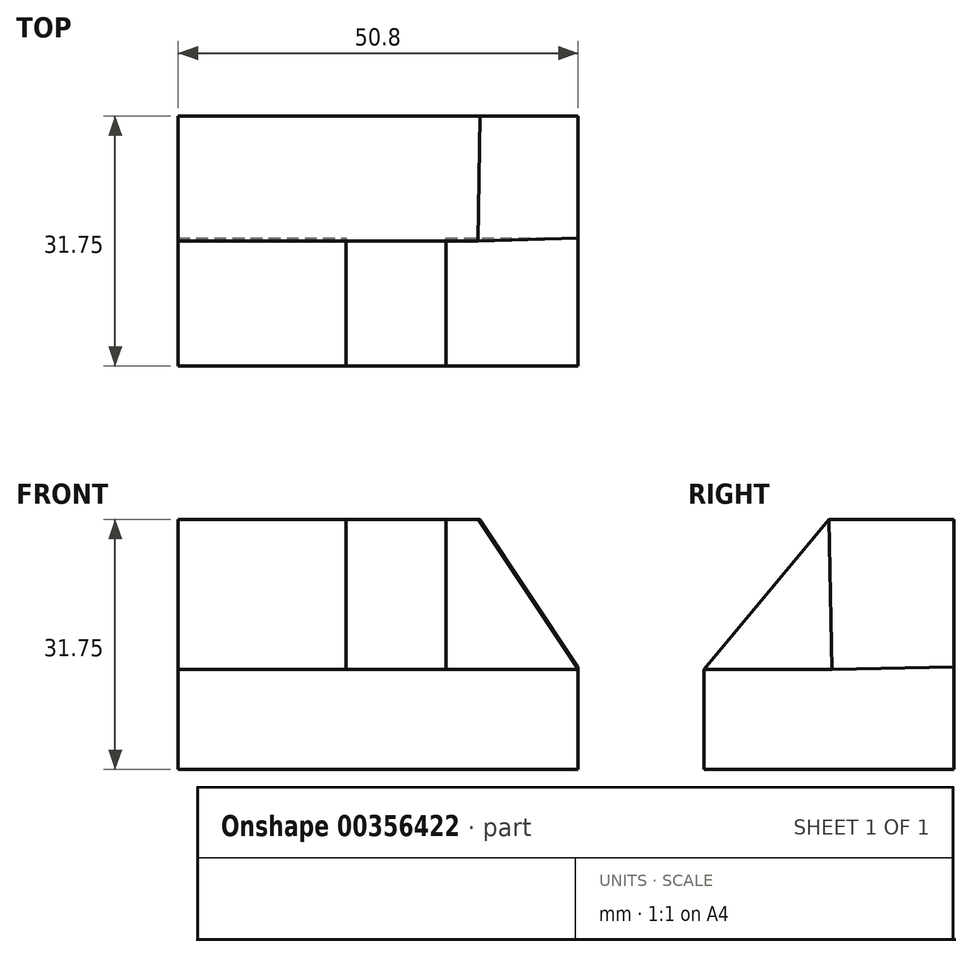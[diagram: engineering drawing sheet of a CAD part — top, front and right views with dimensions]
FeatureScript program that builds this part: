
annotation { "Feature Type Name" : "Feature", "Feature Type Description" : "" }
export const myFeature = defineFeature(function(context is Context, id is Id, definition is map)
    precondition{}
    {
        {
            var Q0;
            Q0=qCreatedBy(makeId("Front.planeOp"),FACE);
            var sketch = newSketch(context, id + "F0", { "sketchPlane" : qUnion([Q0])});
            skLineSegment(sketch, "E0", {"start": v(0, 31.75) * mm, "end": v(0, 0) * mm});
            skLineSegment(sketch, "E1", {"start": v(0, 0) * mm, "end": v(50.8, 0) * mm});
            skLineSegment(sketch, "E2", {"start": v(50.8, 0) * mm, "end": v(50.8, 31.75) * mm});
            skLineSegment(sketch, "E3", {"start": v(50.8, 31.75) * mm, "end": v(0, 31.75) * mm});
            skSolve(sketch);
        }
        {
            var Q0;
            Q0 = qSketchRegion(id + "F0", true);
            extrude(context, id + "F1", {"entities" : qUnion([Q0]), "depth" : 31.75 * mm});
        }
        {
            var Q0;
            Q0=makeQuery(id+"F1.opExtrude","SWEPT_FACE",FACE,{"disambiguationData":[OSD([sQuery(id+"F0.wireOp",EDGE,"E2")])]});
            var sketch = newSketch(context, id + "F2", { "sketchPlane" : qUnion([Q0])});
            skLineSegment(sketch, "E4", {"start": v(-31.75, 12.7) * mm, "end": v(-15.87, 31.75) * mm});
            skSolve(sketch);
        }
        {
            var Q0;
            Q0 = qSketchRegion(id + "F2", true);
            var Q1;
            {var subQ0=sQuery(id+"F2.wireOp",EDGE,"E4");Q1=makeQuery(id+"F2.imprint","IMPRINT",FACE,{"disambiguationData":[TD([[makeQuery(id+"F2.imprint","IMPRINT",EDGE,{"derivedFrom":subQ0}),1.0]])]});}
            extrude(context, id + "F3", {"entities" : qUnion([Q0, Q1]), "operationType" : NewBodyOperationType.REMOVE, "oppositeDirection" : true, "depth" : 50.8 * mm});
        }
        {
            var Q0;
            Q0=makeQuery(id+"F1.opExtrude","SWEPT_FACE",FACE,{"disambiguationData":[OSD([sQuery(id+"F0.wireOp",EDGE,"E2")])]});
            var sketch = newSketch(context, id + "F4", { "sketchPlane" : qUnion([Q0])});
            skLineSegment(sketch, "E5", {"start": v(-31.75, 12.7) * mm, "end": v(-15.48, 12.7) * mm});
            skLineSegment(sketch, "E6", {"start": v(-15.48, 12.7) * mm, "end": v(-15.88, 31.75) * mm});
            skSolve(sketch);
        }
        {
            var Q0;
            Q0=makeQuery(id+"F4.imprint","IMPRINT",FACE,{"disambiguationData":[TD([[makeQuery(id+"F4.imprint","IMPRINT",EDGE,{"derivedFrom":sQuery(id+"F4.wireOp",EDGE,"E5")}),1.0]])]});
            extrude(context, id + "F5", {"entities" : qUnion([Q0]), "operationType" : NewBodyOperationType.REMOVE, "oppositeDirection" : true, "depth" : 50.8 * mm});
        }
        {
            var Q0;
            Q0=makeQuery(id+"F5.boolean.opBoolean","COPY",FACE,{"derivedFrom":makeQuery(id+"F5.opExtrude","SWEPT_FACE",FACE,{"disambiguationData":[OSD([sQuery(id+"F4.wireOp",EDGE,"E6")])]})});
            var sketch = newSketch(context, id + "F6", { "sketchPlane" : qUnion([Q0])});
            skLineSegment(sketch, "E7", {"start": v(50.8, 13.02) * mm, "end": v(38.1, 32.08) * mm});
            skSolve(sketch);
        }
        {
            var Q0;
            Q0 = qSketchRegion(id + "F6", true);
            var Q1;
            {var subQ0=sQuery(id+"F6.wireOp",EDGE,"E7");Q1=makeQuery(id+"F6.imprint","IMPRINT",FACE,{"disambiguationData":[TD([[makeQuery(id+"F6.imprint","IMPRINT",EDGE,{"derivedFrom":subQ0}),-1.0]])]});}
            extrude(context, id + "F7", {"entities" : qUnion([Q0, Q1]), "operationType" : NewBodyOperationType.REMOVE, "oppositeDirection" : true, "depth" : 25.4 * mm});
        }
        {
            var Q0;
            Q0=makeQuery(id+"F5.boolean.opBoolean","COPY",FACE,{"derivedFrom":makeQuery(id+"F5.opExtrude","SWEPT_FACE",FACE,{"disambiguationData":[OSD([sQuery(id+"F4.wireOp",EDGE,"E5")])]})});
            var sketch = newSketch(context, id + "F8", { "sketchPlane" : qUnion([Q0])});
            skLineSegment(sketch, "E8", {"start": v(21.3, -15.48) * mm, "end": v(21.3, -31.75) * mm});
            skLineSegment(sketch, "E9", {"start": v(21.3, -31.75) * mm, "end": v(34, -31.75) * mm});
            skLineSegment(sketch, "E10", {"start": v(34, -31.75) * mm, "end": v(34, -15.48) * mm});
            skLineSegment(sketch, "E11", {"start": v(34, -15.48) * mm, "end": v(21.3, -15.48) * mm});
            skSolve(sketch);
        }
        {
            var Q0;
            Q0 = qSketchRegion(id + "F8", true);
            extrude(context, id + "F9", {"entities" : qUnion([Q0]), "operationType" : NewBodyOperationType.ADD, "depth" : 19.05 * mm});
        }
        {
            var Q0;
            Q0=makeQuery(id+"F9.opExtrude","SWEPT_FACE",FACE,{"disambiguationData":[OSD([sQuery(id+"F8.wireOp",EDGE,"E10")])]});
            var sketch = newSketch(context, id + "F10", { "sketchPlane" : qUnion([Q0])});
            skLineSegment(sketch, "E12", {"start": v(-15.88, 31.75) * mm, "end": v(-31.75, 12.7) * mm});
            skSolve(sketch);
        }
        {
            var Q0;
            Q0 = qSketchRegion(id + "F10", true);
            var Q1;
            Q1=makeQuery(id+"F10.imprint","IMPRINT",FACE,{"disambiguationData":[TD([[makeQuery(id+"F10.imprint","IMPRINT",EDGE,{"derivedFrom":sQuery(id+"F10.wireOp",EDGE,"E12")}),-1.0]])]});
            extrude(context, id + "F11", {"entities" : qUnion([Q0, Q1]), "operationType" : NewBodyOperationType.REMOVE, "oppositeDirection" : true, "depth" : 25.4 * mm});
        }
    });
